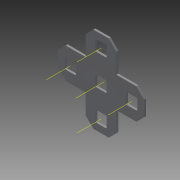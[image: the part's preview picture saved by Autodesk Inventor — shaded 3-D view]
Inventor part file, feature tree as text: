
AUTODESK INVENTOR PART (.ipt)
format: ipt  version: 2015 (Build 190159000, 159)  size: 176,640 bytes
history: native  units: in
note: dims shown in document units (in); Inventor stores cm internally (conversion verified against a paired STEP export)
features: other x8, pattern_linear x2, imported_body x1
ambient origin geometry x8: Origin, YZ Plane, XZ Plane, XY Plane, X Axis, Y Axis, Z Axis, Center Point
bodies: Body1 (feature_tree)
feature tree (11):
  other  "Plus Gusset"
  parser-record x1  (decoder bookkeeping rows leaked as tree rows — omitted from the tree; the rows remain in map.json)
  other  "main axis"
  pattern_linear  "vert axes"  Count1=3 Spacing1=0.5in
  pattern_linear  "horiz axes"  Count1=3 Spacing1=0.5in
  imported_body  "Base1"
  other  "Work Point1"
  other  "Work Axis2"
  other  "Work Axis3"
  other  "Work Axis4"
  other  "Work Axis5"
